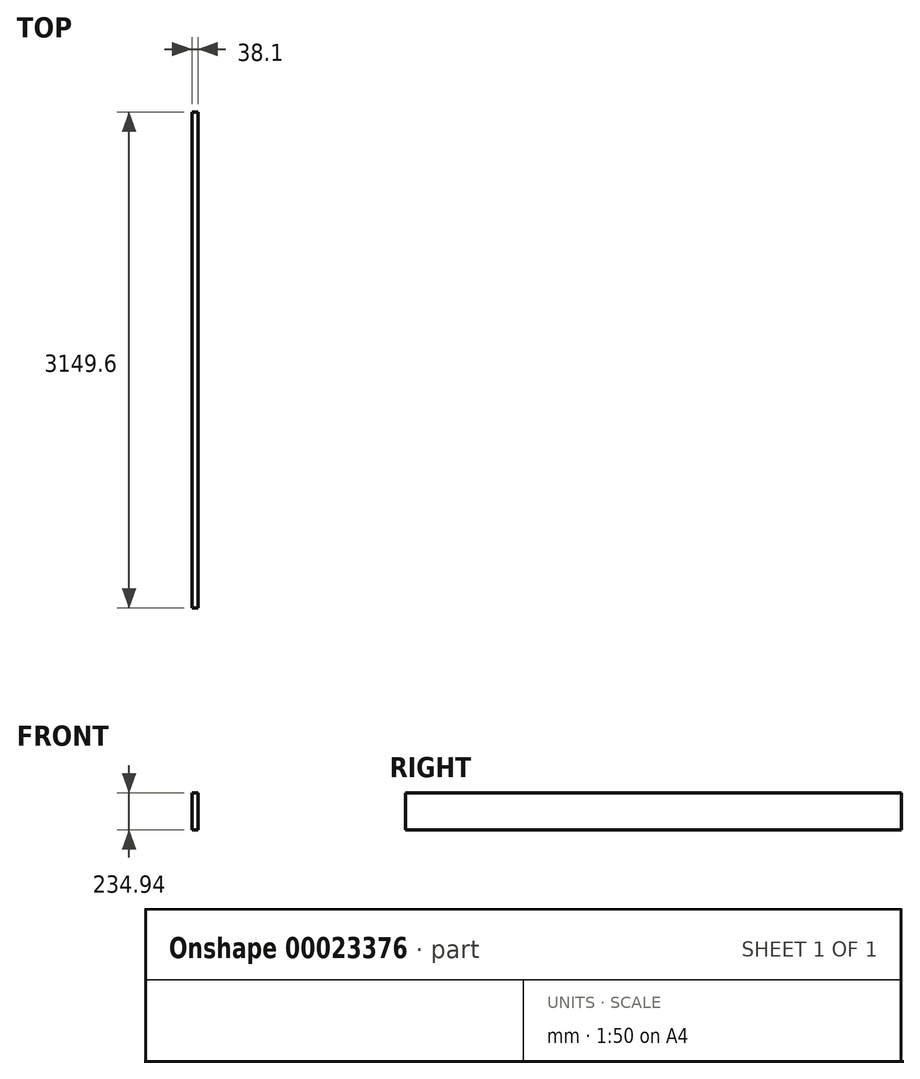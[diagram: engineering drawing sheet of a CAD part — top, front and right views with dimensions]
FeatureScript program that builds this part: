
annotation { "Feature Type Name" : "Feature", "Feature Type Description" : "" }
export const myFeature = defineFeature(function(context is Context, id is Id, definition is map)
    precondition{}
    {
        {
            var Q0;
            Q0=qCreatedBy(makeId("Front.planeOp"),FACE);
            var sketch = newSketch(context, id + "F0", { "sketchPlane" : qUnion([Q0])});
            skLineSegment(sketch, "E0.rect.bottom", {"start": v(-19.05, -117.47) * mm, "end": v(19.05, -117.47) * mm});
            skLineSegment(sketch, "E0.rect.top", {"start": v(-19.05, 117.48) * mm, "end": v(19.05, 117.48) * mm});
            skLineSegment(sketch, "E0.rect.left", {"start": v(-19.05, -117.47) * mm, "end": v(-19.05, 117.47) * mm});
            skLineSegment(sketch, "E0.rect.right", {"start": v(19.05, -117.47) * mm, "end": v(19.05, 117.48) * mm});
            skPoint(sketch, "E0.rect.middle", {"position": v(0, 0) * mm});
            skSolve(sketch);
        }
        {
            var Q0;
            Q0=makeQuery(id+"F0.imprint","IMPRINT",FACE,{"disambiguationData":[TD([[makeQuery(id+"F0.imprint","IMPRINT",EDGE,{"derivedFrom":sQuery(id+"F0.wireOp",EDGE,"E0.rect.bottom")}),1.0]])]});
            extrude(context, id + "F1", {"entities" : qUnion([Q0]), "endBound" : BoundingType.SYMMETRIC, "depth" : 3149.6 * mm});
        }
    });
